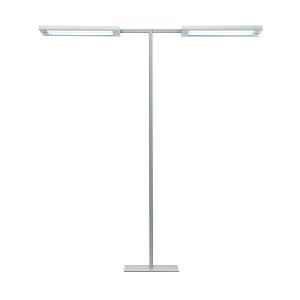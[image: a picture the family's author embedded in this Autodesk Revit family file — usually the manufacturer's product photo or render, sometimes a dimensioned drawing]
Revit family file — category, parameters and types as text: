
# Revit family: lavigo_-_dps_28000_vtl_r_g2_-_twin-t_00800442_2f1e
name_source: partatom
category: Lighting Fixtures
units: mm (PartAtom-declared; Revit-internal decimal feet)

## family parameters
Cut with Voids When Loaded = No
Host = Face
Light Source = No
Part Type = Normal
Room Calculation Point = No
Round Connector Dimension = Use Diameter
Shared = No

## types (1)
- LAVIGO - DPS 28000/VTL/R/G2 - TWIN-T (1 x LED VTL, 14250 lm, 3000-6500K)
    Apparent Load = 200 VA
    Approval mark = CE
    CIE Flux Codes = 60 87 97 12 100
    Color Rendering = 80-89
    Color Temperature = 3000-6500K
    Default Elevation = 1800 mm
    Description = DPS 28000/VTL/R/G2|Free-standing luminaire|light source: LED  3000-6500 K  Energy efficiency category A/A+/A++|LED  4000 K 4000 K Energy efficiency category A/A+/A++|work equipment: Electronic ballast|connected load: 220-240 V, 50/60 Hz|Power consumption: approx. 200 W|standby: approx. 0,50|power factor: approx. 0,966|luminous flux: 28500 lm|luminous efficacy: 142 lm/W|light distribution: Direct/indirect|direct ratio: approx. 12 %|color rendering index (CRI): >= 80|technology: Presence and daylight sensor control (PIR)|operation: Multi-function switch, Touch-LED|luminaire body|material: Steel/plastic|surface: Painted|colour: Silver metallic|lamp cover: Acrylic (PMMA), Satine|tubular section|material: |Form: Tubular section upright|colour of tubular section: Silver metallic|luminaire base|Form: Rectangular flat|weight (net): approx. 28.4 kg|mains lead: 3.00 m Mains plug CEE 7/VII|Fastening: Floor standing base|decorative contrast side parts: Flint grey|glare control: Prism aperture|luminance(L65): <= 3000 cd/m|unified glare rating(4H 8H): <=  16|special features: Luminaire head detachable, Direct light component with edge light and light-guide technology for homogenous light exit, Flicker-free, Integrated light and presence sensor PIR, Integrated light management for biodynamic light VTL, Retrofittable with TALK module, Separated, direct and indirect light individually adjustable|
    Frequency = 50 Hz
    Height = 36 mm
    Lamp = 1 x LED VTL
    Lamp Light Flux = 14250 lm
    Lamp count = 1
    Length = 675 mm
    Luminous efficacy = 143 lm/W
    Manufacturer = Waldmann
    ModVariant = No
    Model = 00800442
    Mounting Place = Floor
    Mounting Type = Freestanding
    Number of Poles = 1
    OnlyDefault = Yes
    Power Factor = 1
    Product Name = LAVIGO - DPS 28000/VTL/R/G2 - TWIN-T
    Product group = Free standing luminaire
    ProductGroupID = 13
    Protection Class = Protection class I
    Protection Degree = IP 20
    RLX_Detail_Level = 1
    RLX_Emergency_Light_Flux = 0 lm
    RLX_Emergency_Type = 0
    RLX_Emergency_Type_DB = No
    RlxData = <blob elided: 33573 chars, md5=cf9c8d23>
    Socket = socket
    Standby Power = 0 W
    System Light Flux = 28500 lm
    System Power = 200 W
    Type Comments = Product without accessories
    Type Image = 121712000-00642698.jpg
    URL = http://relux.com
    VarID = ---
    Voltage = 230 V
    Voltage Range = 220-240 V
    Weight = 0.00 kg
    Width = 350 mm

## geometry (parser evidence)
native form markers: Blend x4, Sweep x21
no freeform markers — native parametric forms only
